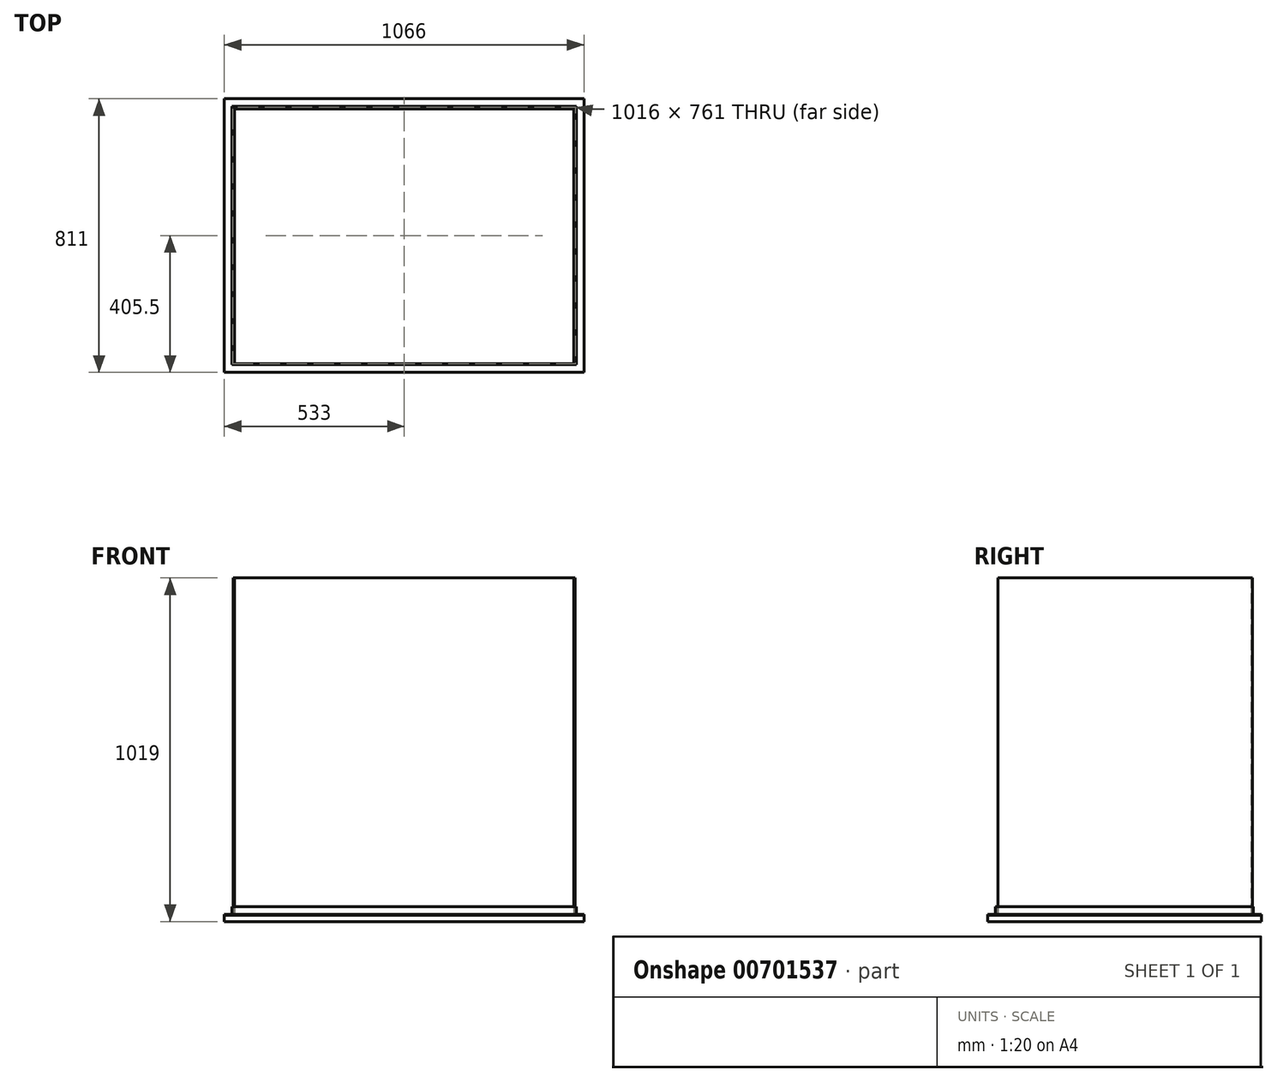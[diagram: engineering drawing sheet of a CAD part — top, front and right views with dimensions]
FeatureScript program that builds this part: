
annotation { "Feature Type Name" : "Feature", "Feature Type Description" : "" }
export const myFeature = defineFeature(function(context is Context, id is Id, definition is map)
    precondition{}
    {
        {
            var Q0;
            Q0=qCreatedBy(makeId("Top.planeOp"),FACE);
            var sketch = newSketch(context, id + "F0", { "sketchPlane" : qUnion([Q0])});
            skLineSegment(sketch, "E0.bottom", {"start": v(-502.5, 375) * mm, "end": v(502.5, 375) * mm});
            skLineSegment(sketch, "E0.left", {"start": v(-502.5, 375) * mm, "end": v(-502.5, -375) * mm});
            skLineSegment(sketch, "E0.right", {"start": v(502.5, 375) * mm, "end": v(502.5, -375) * mm});
            skPoint(sketch, "E0.middle", {"position": v(0, 0) * mm});
            skLineSegment(sketch, "E1.0", {"start": v(-507, 379.5) * mm, "end": v(507, 379.5) * mm});
            skLineSegment(sketch, "E1.1", {"start": v(-507, 379.5) * mm, "end": v(-507, -375) * mm});
            skLineSegment(sketch, "E1.3", {"start": v(507, 379.5) * mm, "end": v(507, -375) * mm});
            skLineSegment(sketch, "E2", {"start": v(-502.5, -375) * mm, "end": v(-507, -375) * mm});
            skLineSegment(sketch, "E3", {"start": v(502.5, -375) * mm, "end": v(507, -375) * mm});
            skSolve(sketch);
        }
        {
            var Q0;
            Q0=qCreatedBy(makeId("Front.planeOp"),FACE);
            var sketch = newSketch(context, id + "F1", { "sketchPlane" : qUnion([Q0])});
            skLineSegment(sketch, "E4", {"start": v(-533, 0) * mm, "end": v(-508, 0) * mm});
            skLineSegment(sketch, "E5", {"start": v(-508, 0) * mm, "end": v(-508, 25) * mm});
            skLineSegment(sketch, "E6.0", {"start": v(-510, 2) * mm, "end": v(-510, 25) * mm});
            skLineSegment(sketch, "E6.1", {"start": v(-533, 2) * mm, "end": v(-510, 2) * mm});
            skLineSegment(sketch, "E7", {"start": v(-533, 2) * mm, "end": v(-533, 0) * mm});
            skLineSegment(sketch, "E8", {"start": v(-510, 25) * mm, "end": v(-508, 25) * mm});
            skSolve(sketch);
        }
        {
            var Q0;
            Q0=qCreatedBy(makeId("Top.planeOp"),FACE);
            var sketch = newSketch(context, id + "F2", { "sketchPlane" : qUnion([Q0])});
            skLineSegment(sketch, "E9.bottom", {"start": v(-508, -380.5) * mm, "end": v(508, -380.5) * mm});
            skLineSegment(sketch, "E9.top", {"start": v(-508, 380.5) * mm, "end": v(508, 380.5) * mm});
            skLineSegment(sketch, "E9.left", {"start": v(-508, -380.5) * mm, "end": v(-508, 380.5) * mm});
            skLineSegment(sketch, "E9.right", {"start": v(508, -380.5) * mm, "end": v(508, 380.5) * mm});
            skPoint(sketch, "E9.middle", {"position": v(0, 0) * mm});
            skSolve(sketch);
        }
        {
            var Q0;
            Q0=makeQuery(id+"F1.imprint","IMPRINT",FACE,{"disambiguationData":[TD([[makeQuery(id+"F1.imprint","IMPRINT",EDGE,{"derivedFrom":sQuery(id+"F1.wireOp",EDGE,"E4")}),1.0]])]});
            var Q1;
            Q1=sQuery(id+"F2.wireOp",EDGE,"E9.left");
            var Q2;
            Q2=sQuery(id+"F2.wireOp",EDGE,"E9.top");
            var Q3;
            Q3=sQuery(id+"F2.wireOp",EDGE,"E9.right");
            var Q4;
            Q4=sQuery(id+"F2.wireOp",EDGE,"E9.bottom");
            sweep(context, id + "F3", {"profiles" : qUnion([Q0]), "path" : qUnion([Q1, Q2, Q3, Q4])});
        }
        {
            var Q0;
            Q0=qCreatedBy(makeId("Top.planeOp"),FACE);
            var sketch = newSketch(context, id + "F4", { "sketchPlane" : qUnion([Q0])});
            skLineSegment(sketch, "E10.bottom", {"start": v(-533, 405.5) * mm, "end": v(533, 405.5) * mm});
            skLineSegment(sketch, "E10.top", {"start": v(-533, -405.5) * mm, "end": v(533, -405.5) * mm});
            skLineSegment(sketch, "E10.left", {"start": v(-533, 405.5) * mm, "end": v(-533, -405.5) * mm});
            skLineSegment(sketch, "E10.right", {"start": v(533, 405.5) * mm, "end": v(533, -405.5) * mm});
            skPoint(sketch, "E10.middle", {"position": v(0, 0) * mm});
            skSolve(sketch);
        }
        {
            var Q0;
            Q0 = qSketchRegion(id + "F4", true);
            extrude(context, id + "F5", {"entities" : qUnion([Q0]), "oppositeDirection" : true, "depth" : 19 * mm, "offsetDistance" : 25 * mm});
        }
        {
            var Q0;
            Q0=makeQuery(id+"F0.imprint","IMPRINT",FACE,{"disambiguationData":[TD([[makeQuery(id+"F0.imprint","IMPRINT",EDGE,{"derivedFrom":sQuery(id+"F0.wireOp",EDGE,"E0.bottom")}),1.0]])]});
            extrude(context, id + "F6", {"entities" : qUnion([Q0]), "operationType" : NewBodyOperationType.ADD, "depth" : 1000 * mm, "offsetDistance" : 25 * mm});
        }
    });
